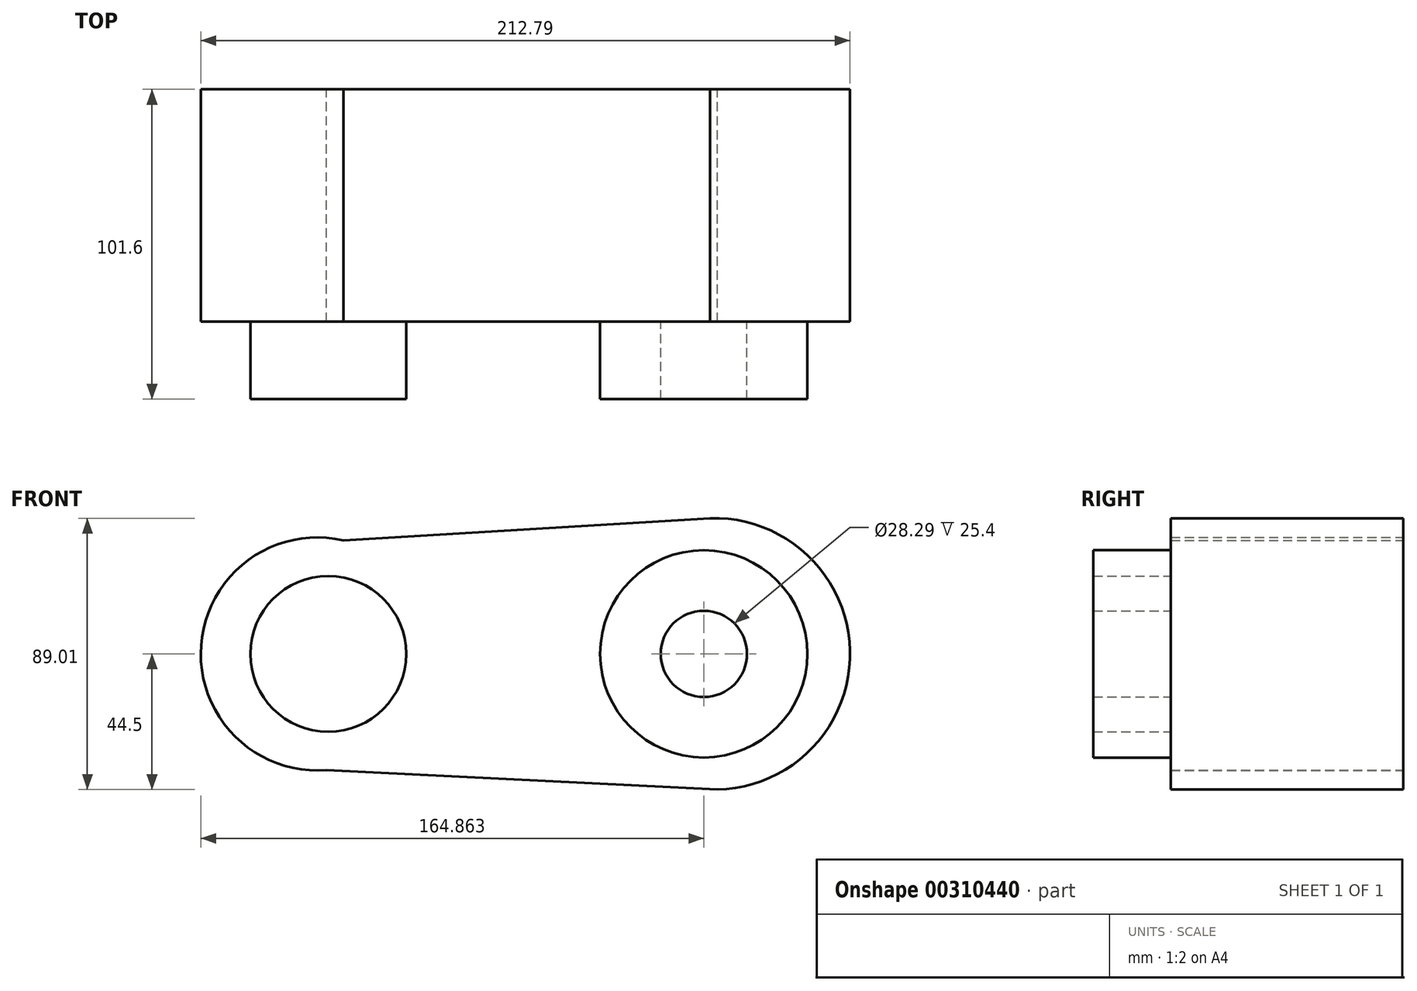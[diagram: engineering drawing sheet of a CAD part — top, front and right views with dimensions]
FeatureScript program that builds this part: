
annotation { "Feature Type Name" : "Feature", "Feature Type Description" : "" }
export const myFeature = defineFeature(function(context is Context, id is Id, definition is map)
    precondition{}
    {
        {
            var Q0;
            Q0=qCreatedBy(makeId("Front.planeOp"),FACE);
            var sketch = newSketch(context, id + "F0", { "sketchPlane" : qUnion([Q0])});
            skCircle(sketch, "E0", {"center": v(-68.04, 0) * mm, "radius": 38.2 * mm});
            skCircle(sketch, "E1", {"center": v(62.05, 0) * mm, "radius": 44.51 * mm});
            skLineSegment(sketch, "E2", {"start": v(-59.5, 37.23) * mm, "end": v(60.73, 44.5) * mm});
            skLineSegment(sketch, "E3", {"start": v(-65.05, -38.08) * mm, "end": v(63.1, -44.5) * mm});
            skCircle(sketch, "E4", {"center": v(-68.04, 0) * mm, "radius": 13.86 * mm});
            skCircle(sketch, "E5", {"center": v(62.05, 0) * mm, "radius": 7.93 * mm});
            skSolve(sketch);
        }
        {
            var Q0;
            {var subQ0=sQuery(id+"F0.wireOp",EDGE,"E2");var subQ1=sQuery(id+"F0.wireOp",EDGE,"E0");var subQ2=makeQuery(id+"F0.imprint","INTERSECT",VERTEX,{"derivedFrom":[subQ1,subQ0]});Q0=makeQuery(id+"F0.imprint","IMPRINT",FACE,{"disambiguationData":[TD([[makeQuery(id+"F0.imprint","IMPRINT",EDGE,{"disambiguationData":[TD([[subQ2,1.0]])],"derivedFrom":subQ1}),-1.0]])]});}
            var Q1;
            Q1=makeQuery(id+"F0.imprint","IMPRINT",FACE,{"disambiguationData":[TD([[makeQuery(id+"F0.imprint","IMPRINT",EDGE,{"derivedFrom":sQuery(id+"F0.wireOp",EDGE,"E4")}),-1.0]])]});
            var Q2;
            Q2=makeQuery(id+"F0.imprint","IMPRINT",FACE,{"disambiguationData":[TD([[makeQuery(id+"F0.imprint","IMPRINT",EDGE,{"derivedFrom":sQuery(id+"F0.wireOp",EDGE,"E4")}),1.0]])]});
            var Q3;
            Q3=makeQuery(id+"F0.imprint","IMPRINT",FACE,{"disambiguationData":[TD([[makeQuery(id+"F0.imprint","IMPRINT",EDGE,{"derivedFrom":sQuery(id+"F0.wireOp",EDGE,"E5")}),-1.0]])]});
            var Q4;
            Q4=makeQuery(id+"F0.imprint","IMPRINT",FACE,{"disambiguationData":[TD([[makeQuery(id+"F0.imprint","IMPRINT",EDGE,{"derivedFrom":sQuery(id+"F0.wireOp",EDGE,"E5")}),1.0]])]});
            extrude(context, id + "F1", {"entities" : qUnion([Q0, Q1, Q2, Q3, Q4]), "depth" : 76.2 * mm});
        }
        {
            var Q0;
            Q0=makeQuery(id+"F1.opExtrude","CAP_FACE",FACE,{"disambiguationData":[OSD([sQuery(id+"F0.wireOp",EDGE,"E0"),sQuery(id+"F0.wireOp",EDGE,"E1"),sQuery(id+"F0.wireOp",EDGE,"E2"),sQuery(id+"F0.wireOp",EDGE,"E3")])],"isStart":false});
            var sketch = newSketch(context, id + "F2", { "sketchPlane" : qUnion([Q0])});
            skCircle(sketch, "E6", {"center": v(58.63, 0) * mm, "radius": 33.98 * mm});
            skCircle(sketch, "E7", {"center": v(58.63, 0) * mm, "radius": 14.15 * mm});
            skCircle(sketch, "E8", {"center": v(-64.46, 0) * mm, "radius": 25.54 * mm});
            skCircle(sketch, "E9", {"center": v(-64.46, 0) * mm, "radius": 12.14 * mm});
            skSolve(sketch);
        }
        {
            var Q0;
            Q0=makeQuery(id+"F2.imprint","IMPRINT",FACE,{"disambiguationData":[TD([[makeQuery(id+"F2.imprint","IMPRINT",EDGE,{"derivedFrom":sQuery(id+"F2.wireOp",EDGE,"E6")}),1.0]])]});
            var Q1;
            Q1=makeQuery(id+"F2.imprint","IMPRINT",FACE,{"disambiguationData":[TD([[makeQuery(id+"F2.imprint","IMPRINT",EDGE,{"derivedFrom":sQuery(id+"F2.wireOp",EDGE,"E8")}),1.0]])]});
            var Q2;
            Q2=makeQuery(id+"F2.imprint","IMPRINT",FACE,{"disambiguationData":[TD([[makeQuery(id+"F2.imprint","IMPRINT",EDGE,{"derivedFrom":sQuery(id+"F2.wireOp",EDGE,"E9")}),1.0]])]});
            extrude(context, id + "F3", {"entities" : qUnion([Q0, Q1, Q2]), "operationType" : NewBodyOperationType.ADD, "depth" : 25.4 * mm});
        }
    });
